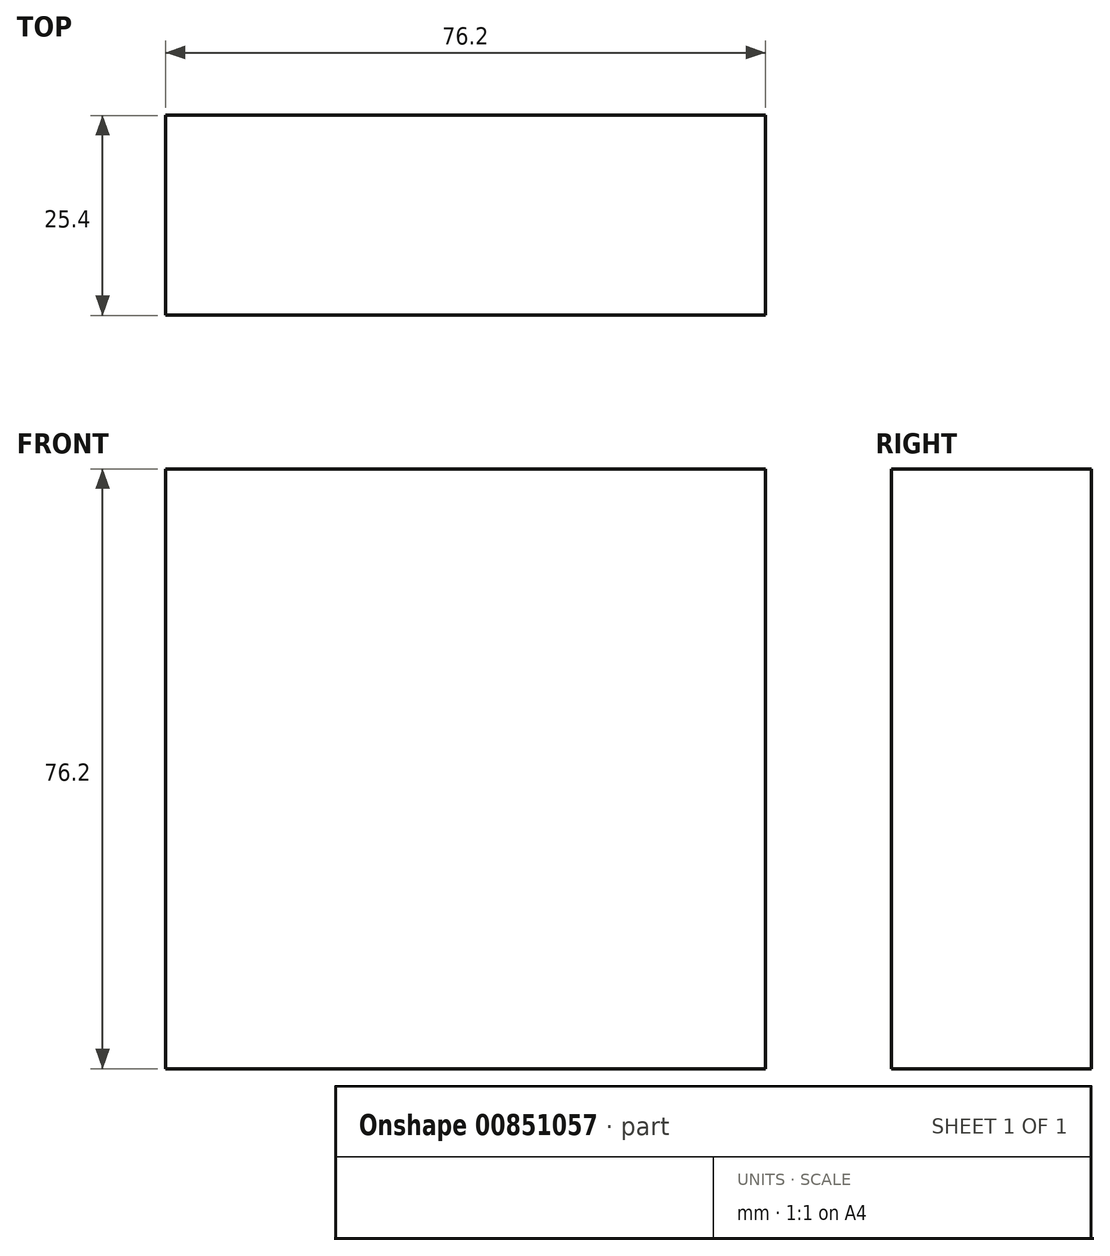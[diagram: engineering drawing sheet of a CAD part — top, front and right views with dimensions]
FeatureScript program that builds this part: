
annotation { "Feature Type Name" : "Feature", "Feature Type Description" : "" }
export const myFeature = defineFeature(function(context is Context, id is Id, definition is map)
    precondition{}
    {
        {
            var Q0;
            Q0=qCreatedBy(makeId("Top.planeOp"),FACE);
            var sketch = newSketch(context, id + "F0", { "sketchPlane" : qUnion([Q0])});
            skLineSegment(sketch, "E0.bottom", {"start": v(-58.75, -55.12) * mm, "end": v(17.45, -55.12) * mm});
            skLineSegment(sketch, "E0.top", {"start": v(-58.75, -29.72) * mm, "end": v(17.45, -29.72) * mm});
            skLineSegment(sketch, "E0.left", {"start": v(-58.75, -55.12) * mm, "end": v(-58.75, -29.72) * mm});
            skLineSegment(sketch, "E0.right", {"start": v(17.45, -55.12) * mm, "end": v(17.45, -29.72) * mm});
            skSolve(sketch);
        }
        {
            var Q0;
            Q0=qSketchRegion(id+"F0",true);
            extrude(context, id + "F1", {"entities" : qUnion([Q0]), "depth" : 76.2 * mm, "offsetDistance" : 25.4 * mm});
        }
    });
